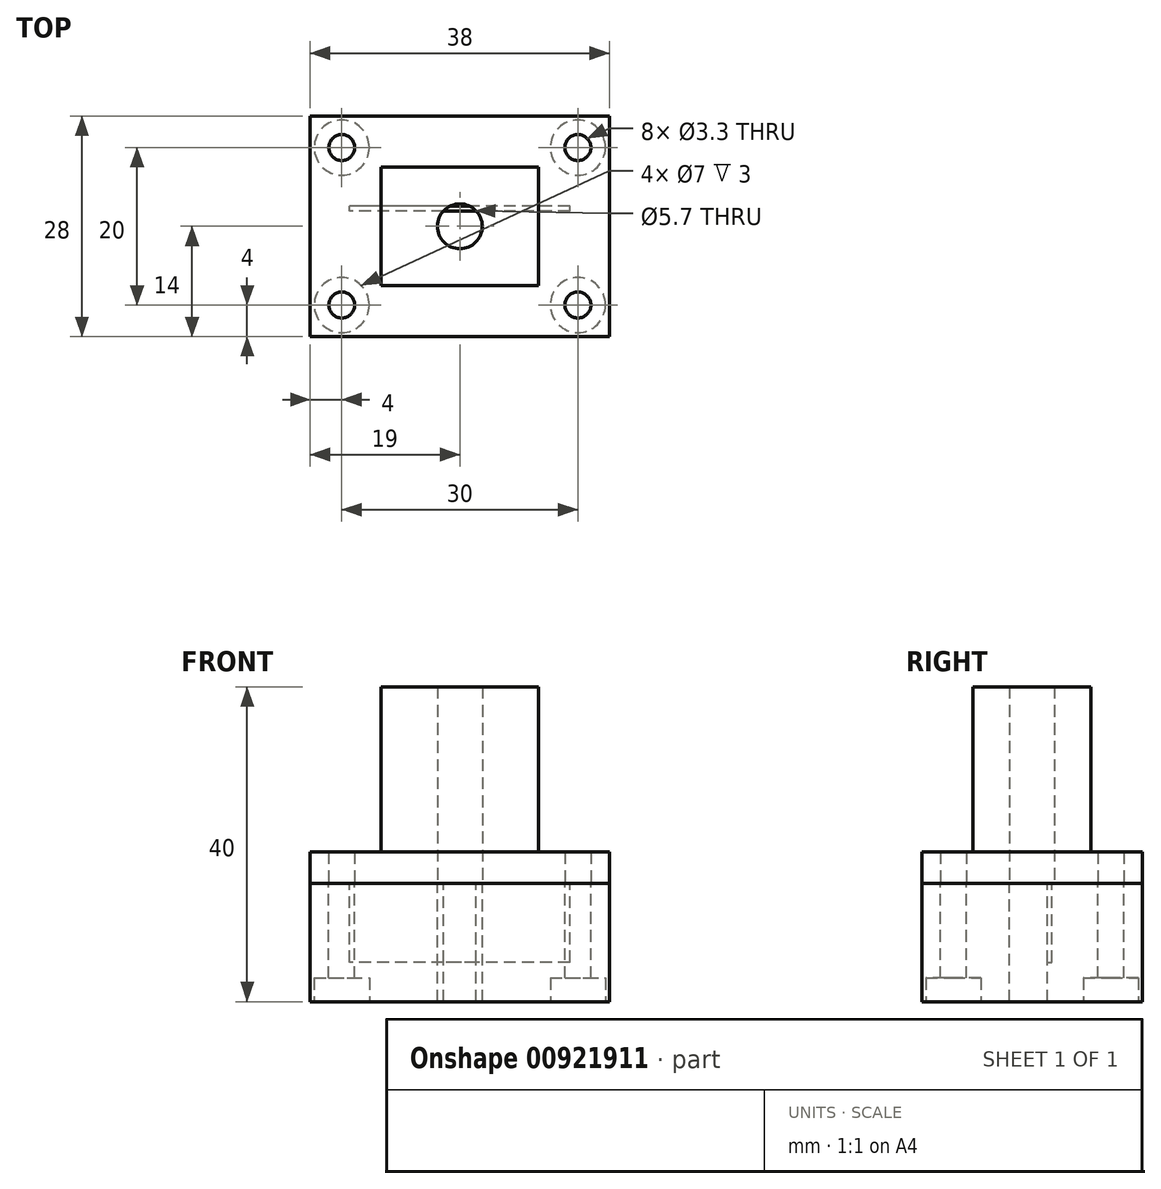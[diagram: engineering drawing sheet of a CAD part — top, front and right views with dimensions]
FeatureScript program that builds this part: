
annotation { "Feature Type Name" : "Feature", "Feature Type Description" : "" }
export const myFeature = defineFeature(function(context is Context, id is Id, definition is map)
    precondition{}
    {
        {
            var Q0;
            Q0=qCreatedBy(makeId("Top.planeOp"),FACE);
            var sketch = newSketch(context, id + "F0", { "sketchPlane" : qUnion([Q0])});
            skCircle(sketch, "E0", {"center": v(0, 0) * mm, "radius": 2.85 * mm});
            skLineSegment(sketch, "E1.bottom", {"start": v(-10, 7.5) * mm, "end": v(10, 7.5) * mm});
            skLineSegment(sketch, "E1.top", {"start": v(-10, -7.5) * mm, "end": v(10, -7.5) * mm});
            skLineSegment(sketch, "E1.left", {"start": v(-10, 7.5) * mm, "end": v(-10, -7.5) * mm});
            skLineSegment(sketch, "E1.right", {"start": v(10, 7.5) * mm, "end": v(10, -7.5) * mm});
            skSolve(sketch);
        }
        {
            var Q0;
            Q0=makeQuery(id+"F0.imprint","IMPRINT",FACE,{"disambiguationData":[TD([[makeQuery(id+"F0.imprint","IMPRINT",EDGE,{"derivedFrom":sQuery(id+"F0.wireOp",EDGE,"E0")}),-1.0]])]});
            extrude(context, id + "F1", {"entities" : qUnion([Q0]), "depth" : 25 * mm, "offsetDistance" : 25 * mm});
        }
        {
            var Q0;
            Q0=makeQuery(id+"F1.opExtrude","CAP_FACE",FACE,{"disambiguationData":[OSD([sQuery(id+"F0.wireOp",EDGE,"E0"),sQuery(id+"F0.wireOp",EDGE,"E1.bottom"),sQuery(id+"F0.wireOp",EDGE,"E1.top"),sQuery(id+"F0.wireOp",EDGE,"E1.left"),sQuery(id+"F0.wireOp",EDGE,"E1.right")])],"isStart":true});
            var sketch = newSketch(context, id + "F2", { "sketchPlane" : qUnion([Q0])});
            skLineSegment(sketch, "E2.bottom", {"start": v(-19, 14) * mm, "end": v(19, 14) * mm});
            skLineSegment(sketch, "E2.top", {"start": v(-19, -14) * mm, "end": v(19, -14) * mm});
            skLineSegment(sketch, "E2.left", {"start": v(-19, 14) * mm, "end": v(-19, -14) * mm});
            skLineSegment(sketch, "E2.right", {"start": v(19, 14) * mm, "end": v(19, -14) * mm});
            skCircle(sketch, "E3", {"center": v(0, 0) * mm, "radius": 2.85 * mm});
            skCircle(sketch, "E4", {"center": v(-15, 10) * mm, "radius": 1.65 * mm});
            skCircle(sketch, "E5.MirrorC", {"center": v(15, 10) * mm, "radius": 1.65 * mm});
            skCircle(sketch, "E6.MirrorC", {"center": v(15, -10) * mm, "radius": 1.65 * mm});
            skCircle(sketch, "E7.MirrorC", {"center": v(-15, -10) * mm, "radius": 1.65 * mm});
            skSolve(sketch);
        }
        {
            var Q0;
            Q0 = qSketchRegion(id + "F2", true);
            extrude(context, id + "F3", {"entities" : qUnion([Q0]), "operationType" : NewBodyOperationType.ADD, "oppositeDirection" : true, "depth" : 4 * mm, "offsetDistance" : 25 * mm});
        }
        {
            var Q0;
            Q0=qCreatedBy(makeId("Top.planeOp"),FACE);
            var sketch = newSketch(context, id + "F4", { "sketchPlane" : qUnion([Q0])});
            skLineSegment(sketch, "E8.bottom", {"start": v(-19, -14) * mm, "end": v(19, -14) * mm});
            skLineSegment(sketch, "E8.top", {"start": v(-19, 14) * mm, "end": v(19, 14) * mm});
            skLineSegment(sketch, "E8.left", {"start": v(-19, -14) * mm, "end": v(-19, 14) * mm});
            skLineSegment(sketch, "E8.right", {"start": v(19, -14) * mm, "end": v(19, 14) * mm});
            skCircle(sketch, "E9", {"center": v(-15, -10) * mm, "radius": 1.65 * mm});
            skCircle(sketch, "E10", {"center": v(-15, 10) * mm, "radius": 1.65 * mm});
            skCircle(sketch, "E11", {"center": v(15, 10) * mm, "radius": 1.65 * mm});
            skCircle(sketch, "E12", {"center": v(15, -10) * mm, "radius": 1.65 * mm});
            skArc(sketch, "E13", {"start": v(-2.08, 1.95) * mm, "mid": v(0, -2.85) * mm, "end": v(2.08, 1.95) * mm});
            skLineSegment(sketch, "E14", {"start": v(-2.08, 1.95) * mm, "end": v(2.08, 1.95) * mm});
            skSolve(sketch);
        }
        {
            var Q0;
            Q0 = qSketchRegion(id + "F4", true);
            extrude(context, id + "F5", {"entities" : qUnion([Q0]), "oppositeDirection" : true, "depth" : 15 * mm, "offsetDistance" : 25 * mm});
        }
        {
            var Q0;
            Q0=makeQuery(id+"F5.opExtrude","CAP_FACE",FACE,{"disambiguationData":[OSD([sQuery(id+"F4.wireOp",EDGE,"E8.bottom"),sQuery(id+"F4.wireOp",EDGE,"E8.top"),sQuery(id+"F4.wireOp",EDGE,"E8.left"),sQuery(id+"F4.wireOp",EDGE,"E8.right"),sQuery(id+"F4.wireOp",EDGE,"E9"),sQuery(id+"F4.wireOp",EDGE,"E10"),sQuery(id+"F4.wireOp",EDGE,"E11"),sQuery(id+"F4.wireOp",EDGE,"E12"),sQuery(id+"F4.wireOp",EDGE,"E13"),sQuery(id+"F4.wireOp",EDGE,"E14")])],"isStart":true});
            var sketch = newSketch(context, id + "F6", { "sketchPlane" : qUnion([Q0])});
            skLineSegment(sketch, "E15.bottom", {"start": v(14, 1.95) * mm, "end": v(-14, 1.95) * mm});
            skLineSegment(sketch, "E15.top", {"start": v(14, 2.55) * mm, "end": v(-14, 2.55) * mm});
            skLineSegment(sketch, "E15.left", {"start": v(14, 1.95) * mm, "end": v(14, 2.55) * mm});
            skLineSegment(sketch, "E15.right", {"start": v(-14, 1.95) * mm, "end": v(-14, 2.55) * mm});
            skSolve(sketch);
        }
        {
            var Q0;
            Q0 = qSketchRegion(id + "F6", true);
            extrude(context, id + "F7", {"entities" : qUnion([Q0]), "operationType" : NewBodyOperationType.REMOVE, "oppositeDirection" : true, "depth" : 10 * mm, "offsetDistance" : 25 * mm});
        }
        {
            var Q0;
            Q0=makeQuery(id+"F5.opExtrude","CAP_FACE",FACE,{"disambiguationData":[OSD([sQuery(id+"F4.wireOp",EDGE,"E8.bottom"),sQuery(id+"F4.wireOp",EDGE,"E8.top"),sQuery(id+"F4.wireOp",EDGE,"E8.left"),sQuery(id+"F4.wireOp",EDGE,"E8.right"),sQuery(id+"F4.wireOp",EDGE,"E9"),sQuery(id+"F4.wireOp",EDGE,"E10"),sQuery(id+"F4.wireOp",EDGE,"E11"),sQuery(id+"F4.wireOp",EDGE,"E12"),sQuery(id+"F4.wireOp",EDGE,"E13"),sQuery(id+"F4.wireOp",EDGE,"E14")])],"isStart":false});
            var sketch = newSketch(context, id + "F8", { "sketchPlane" : qUnion([Q0])});
            skCircle(sketch, "E16", {"center": v(15, -10) * mm, "radius": 3.5 * mm});
            skCircle(sketch, "E17.MirrorC", {"center": v(-15, -10) * mm, "radius": 3.5 * mm});
            skCircle(sketch, "E18.MirrorC", {"center": v(-15, 10) * mm, "radius": 3.5 * mm});
            skCircle(sketch, "E19.MirrorC", {"center": v(15, 10) * mm, "radius": 3.5 * mm});
            skSolve(sketch);
        }
        {
            var Q0;
            Q0 = qSketchRegion(id + "F8", true);
            extrude(context, id + "F9", {"entities" : qUnion([Q0]), "operationType" : NewBodyOperationType.REMOVE, "oppositeDirection" : true, "depth" : 3 * mm, "offsetDistance" : 25 * mm});
        }
    });
